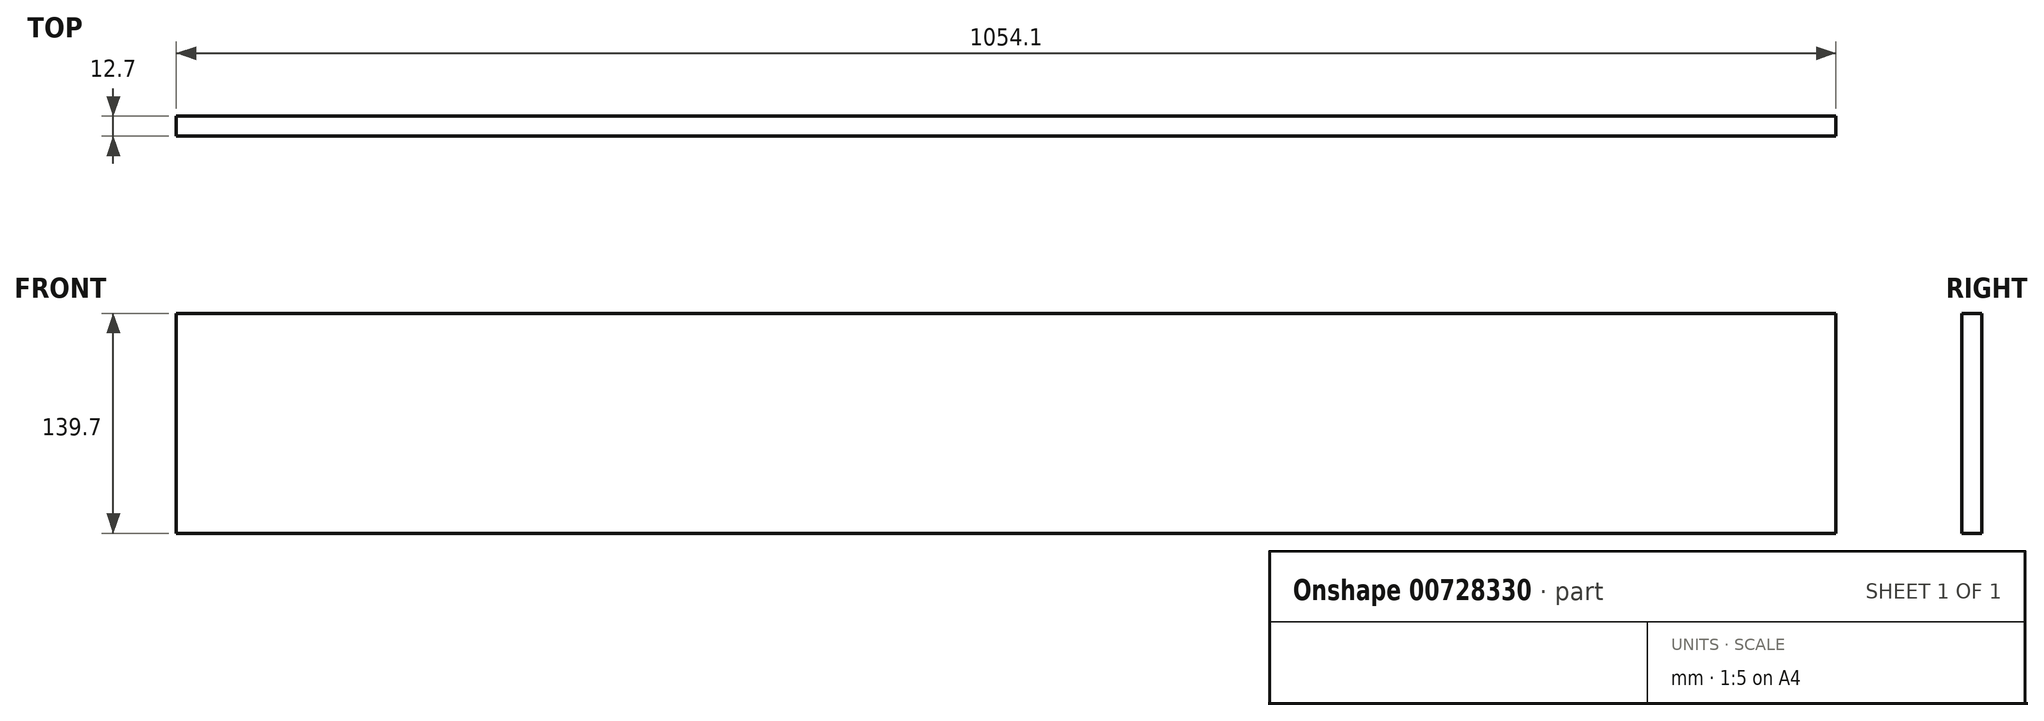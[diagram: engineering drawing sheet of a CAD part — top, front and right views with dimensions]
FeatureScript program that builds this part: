
annotation { "Feature Type Name" : "Feature", "Feature Type Description" : "" }
export const myFeature = defineFeature(function(context is Context, id is Id, definition is map)
    precondition{}
    {
        {
            var Q0;
            Q0=qCreatedBy(makeId("Front.planeOp"),FACE);
            var sketch = newSketch(context, id + "F0", { "sketchPlane" : qUnion([Q0])});
            skLineSegment(sketch, "E0.bottom", {"start": v(-527.05, -69.85) * mm, "end": v(527.05, -69.85) * mm});
            skLineSegment(sketch, "E0.top", {"start": v(-527.05, 69.85) * mm, "end": v(527.05, 69.85) * mm});
            skLineSegment(sketch, "E0.left", {"start": v(-527.05, -69.85) * mm, "end": v(-527.05, 69.85) * mm});
            skLineSegment(sketch, "E0.right", {"start": v(527.05, -69.85) * mm, "end": v(527.05, 69.85) * mm});
            skPoint(sketch, "E0.middle", {"position": v(0, 0) * mm});
            skSolve(sketch);
        }
        {
            var Q0;
            Q0=makeQuery(id+"F0.imprint","IMPRINT",FACE,{"disambiguationData":[TD([[makeQuery(id+"F0.imprint","IMPRINT",EDGE,{"derivedFrom":sQuery(id+"F0.wireOp",EDGE,"E0.bottom")}),1.0]])]});
            extrude(context, id + "F1", {"entities" : qUnion([Q0]), "depth" : 12.7 * mm});
        }
    });
